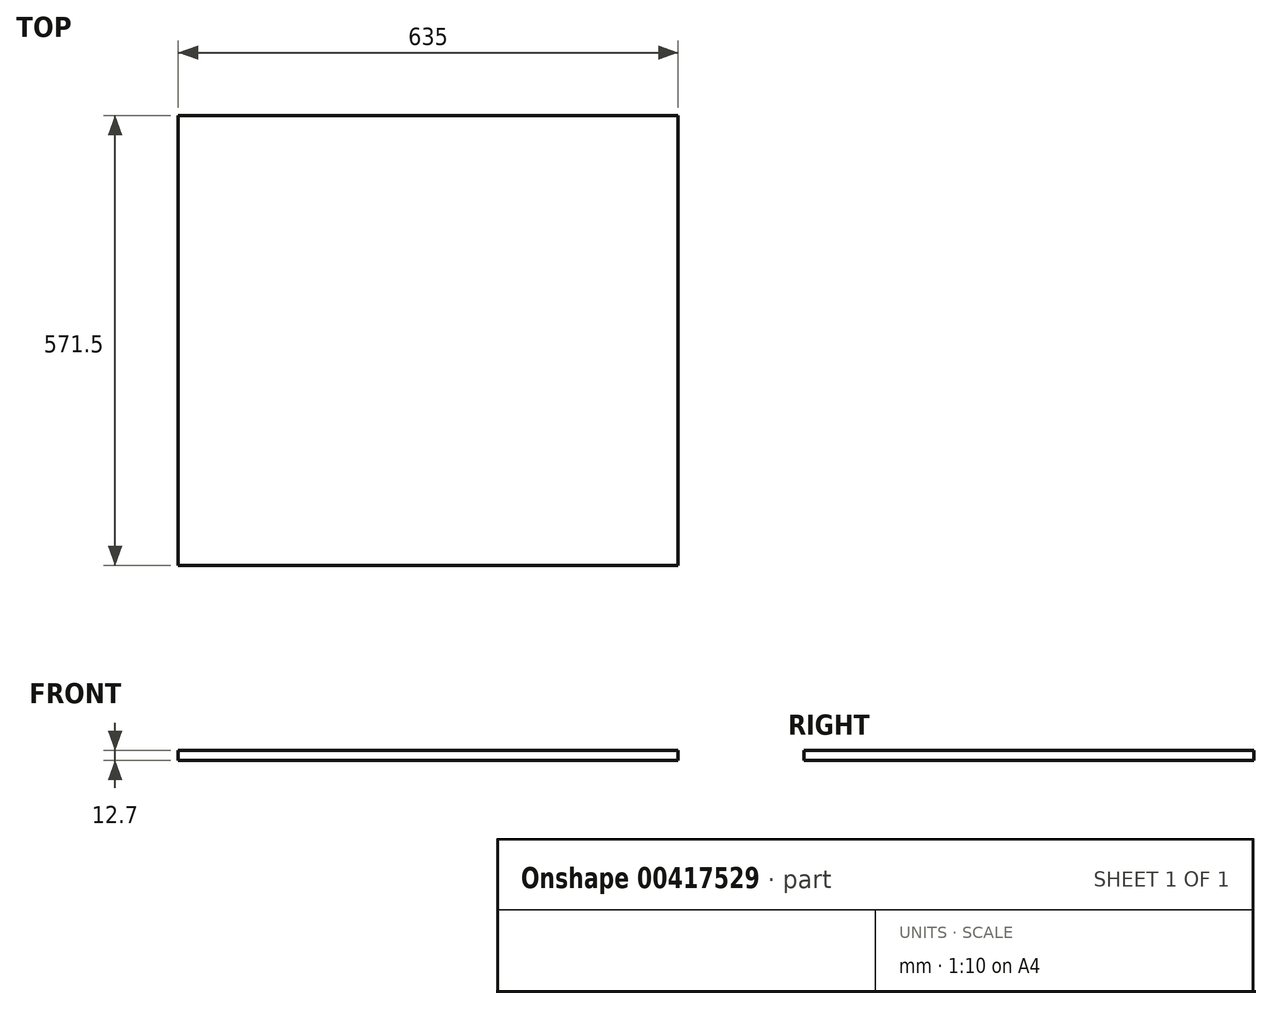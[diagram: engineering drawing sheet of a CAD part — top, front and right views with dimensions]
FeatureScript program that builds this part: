
annotation { "Feature Type Name" : "Feature", "Feature Type Description" : "" }
export const myFeature = defineFeature(function(context is Context, id is Id, definition is map)
    precondition{}
    {
        {
            var Q0;
            Q0=qCreatedBy(makeId("Top.planeOp"),FACE);
            var sketch = newSketch(context, id + "F0", { "sketchPlane" : qUnion([Q0])});
            skLineSegment(sketch, "E0.bottom", {"start": v(-317.5, 285.75) * mm, "end": v(317.5, 285.75) * mm});
            skLineSegment(sketch, "E0.top", {"start": v(-317.5, -285.75) * mm, "end": v(317.5, -285.75) * mm});
            skLineSegment(sketch, "E0.left", {"start": v(-317.5, 285.75) * mm, "end": v(-317.5, -285.75) * mm});
            skLineSegment(sketch, "E0.right", {"start": v(317.5, 285.75) * mm, "end": v(317.5, -285.75) * mm});
            skPoint(sketch, "E0.middle", {"position": v(0, 0) * mm});
            skSolve(sketch);
        }
        {
            var Q0;
            Q0 = qSketchRegion(id + "F0", true);
            extrude(context, id + "F1", {"entities" : qUnion([Q0]), "depth" : 12.7 * mm});
        }
    });
